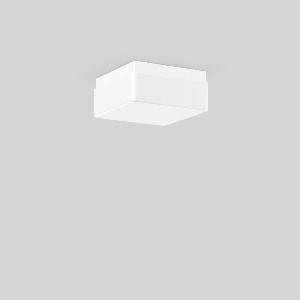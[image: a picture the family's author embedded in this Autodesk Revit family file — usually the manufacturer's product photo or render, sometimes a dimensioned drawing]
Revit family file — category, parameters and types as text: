
# Revit family: quadrat_21128_002_5cfc
name_source: partatom
category: Lighting Fixtures
units: mm (PartAtom-declared; Revit-internal decimal feet)

## family parameters
Cut with Voids When Loaded = No
Host = Face
Light Source = No
Part Type = Normal
Room Calculation Point = No
Round Connector Dimension = Use Diameter
Shared = No

## types (1)
- QUADRAT (1 x QA60/clear E27, 915 lm, 57 W, 3000)
    Apparent Load = 57 VA
    CIE Flux Codes = 35 64 86 74 50
    Color Rendering = 90
    Color Temperature = 3000
    Default Elevation = 1800 mm
    Description = Series: QUADRAT
Square surface-mounted luminaire in classic design. Base: plastic. Opal glass: mouth-blown, satin finish. Diffuser fastening: spring system. Suitable for Ceiling mounting, Wall (surface). IP 43 ceiling mounting, IP 44 wall mounting. 
Colour: white
Length: 240 mm
Width: 240 mm
Height: 110 mm
Lamp: A60
Number of lamps: 1
Wattage: 75 W
Socket: E27
System power: 60 W
Rated luminous flux: 370 lm
Luminous efficiency: 6 lm/W
Control gear: Converter not necessary
Protection class: II
Type of protection: IP 43
    Height = 110 mm
    Lamp = 1 x QA60/clear E27
    Lamp Light Flux = 915 lm
    Lamp Power = 57 W
    Lamp count = 1
    Length = 240 mm
    Lifetime = 3000 h
    Luminous efficacy = 8 lm/W
    Manufacturer = RZB
    ModVariant = No
    Model = 21128.002
    Mounting Place = Ceiling, Wall
    Mounting Type = Surface mounted
    Number of Poles = 1
    OnlyDefault = Yes
    Power Factor = 1
    Product Name = QUADRAT
    Product group = Surface mounted ceiling and wall luminaires
    ProductGroupID = 305
    Protection Class = Protection class II
    Protection Degree = IP 43
    RLX_Detail_Level = 1
    RLX_Emergency_Light_Flux = 0 lm
    RLX_Emergency_Type = 0
    RLX_Emergency_Type_DB = No
    RlxData = <blob elided: 10025 chars, md5=d6f31e1b>
    Socket = E27
    Standby Power = 0 W
    System Light Flux = 460 lm
    System Power = 57 W
    Type Comments = Product without accessories
    Type Image = 21128.002.jpg
    URL = http://relux.com
    VarID = ---
    Voltage = 230 V
    Voltage Range = 220-240 V
    Weight = 0.00 kg
    Width = 240 mm

## geometry (parser evidence)
native form markers: Sweep x11
no freeform markers — native parametric forms only
